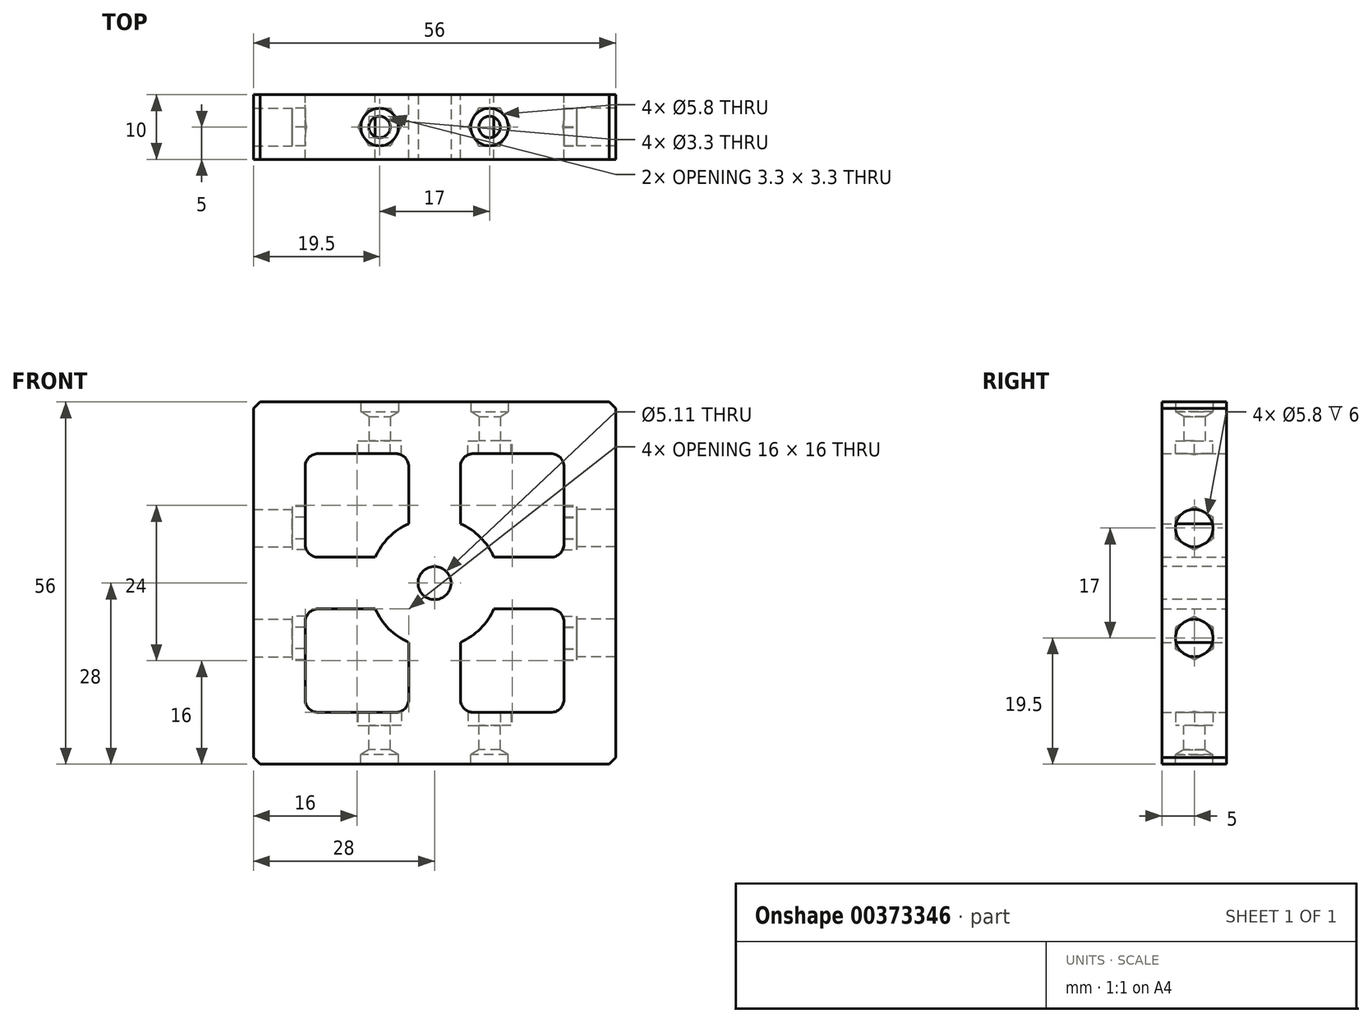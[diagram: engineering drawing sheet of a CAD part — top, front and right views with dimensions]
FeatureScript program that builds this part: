
annotation { "Feature Type Name" : "Feature", "Feature Type Description" : "" }
export const myFeature = defineFeature(function(context is Context, id is Id, definition is map)
    precondition{}
    {
        {
            var Q0;
            Q0=qCreatedBy(makeId("Front.planeOp"),FACE);
            var sketch = newSketch(context, id + "F0", { "sketchPlane" : qUnion([Q0])});
            skLineSegment(sketch, "E0.bottom", {"start": v(28, -28) * mm, "end": v(-28, -28) * mm});
            skLineSegment(sketch, "E0.top", {"start": v(28, 28) * mm, "end": v(-28, 28) * mm});
            skLineSegment(sketch, "E0.left", {"start": v(28, -28) * mm, "end": v(28, 28) * mm});
            skLineSegment(sketch, "E0.right", {"start": v(-28, -28) * mm, "end": v(-28, 28) * mm});
            skPoint(sketch, "E0.middle", {"position": v(0, 0) * mm});
            skLineSegment(sketch, "E1.bottom", {"start": v(18, -20) * mm, "end": v(6, -20) * mm});
            skLineSegment(sketch, "E1.top", {"start": v(18, 20) * mm, "end": v(6, 20) * mm});
            skLineSegment(sketch, "E1.left", {"start": v(20, -18) * mm, "end": v(20, -6) * mm});
            skLineSegment(sketch, "E1.right", {"start": v(-20, 6) * mm, "end": v(-20, 18) * mm});
            skLineSegment(sketch, "E2.left", {"start": v(4, -18) * mm, "end": v(4, 18) * mm});
            skLineSegment(sketch, "E2.right", {"start": v(-4, -18) * mm, "end": v(-4, 18) * mm});
            skLineSegment(sketch, "E3.bottom", {"start": v(18, -4) * mm, "end": v(-18, -4) * mm});
            skLineSegment(sketch, "E3.top", {"start": v(18, 4) * mm, "end": v(-18, 4) * mm});
            skPoint(sketch, "E4", {"position": v(28, -8.5) * mm});
            skPoint(sketch, "E5", {"position": v(28, 8.5) * mm});
            skPoint(sketch, "E6", {"position": v(28, 0) * mm});
            skCircle(sketch, "E7", {"center": v(0, 0) * mm, "radius": 10 * mm});
            skPoint(sketch, "E8.visualSharp", {"position": v(-20, 20) * mm});
            skArc(sketch, "E8.filletArc", {"start": v(-18, 20) * mm, "mid": v(-19.41, 19.41) * mm, "end": v(-20, 18) * mm});
            skPoint(sketch, "E9.visualSharp", {"position": v(20, 20) * mm});
            skArc(sketch, "E9.filletArc", {"start": v(20, 18) * mm, "mid": v(19.41, 19.41) * mm, "end": v(18, 20) * mm});
            skPoint(sketch, "E10.visualSharp", {"position": v(-20, -20) * mm});
            skArc(sketch, "E10.filletArc", {"start": v(-20, -18) * mm, "mid": v(-19.41, -19.41) * mm, "end": v(-18, -20) * mm});
            skPoint(sketch, "E11.visualSharp", {"position": v(20, -20) * mm});
            skArc(sketch, "E11.filletArc", {"start": v(18, -20) * mm, "mid": v(19.41, -19.41) * mm, "end": v(20, -18) * mm});
            skArc(sketch, "E12.filletArc", {"start": v(4, -18) * mm, "mid": v(4.59, -19.41) * mm, "end": v(6, -20) * mm});
            skPoint(sketch, "E13.newPointA", {"position": v(-20, 4) * mm});
            skArc(sketch, "E13.filletArc", {"start": v(-20, 6) * mm, "mid": v(-19.41, 4.59) * mm, "end": v(-18, 4) * mm});
            skArc(sketch, "E14.filletArc", {"start": v(6, 20) * mm, "mid": v(4.59, 19.41) * mm, "end": v(4, 18) * mm});
            skPoint(sketch, "E15.newPointA", {"position": v(20, -4) * mm});
            skArc(sketch, "E15.filletArc", {"start": v(20, -6) * mm, "mid": v(19.41, -4.59) * mm, "end": v(18, -4) * mm});
            skLineSegment(sketch, "E16", {"start": v(-6, -20) * mm, "end": v(-18, -20) * mm});
            skLineSegment(sketch, "E17", {"start": v(-20, -18) * mm, "end": v(-20, -6) * mm});
            skLineSegment(sketch, "E18", {"start": v(-18, 20) * mm, "end": v(-6, 20) * mm});
            skLineSegment(sketch, "E19", {"start": v(20, 18) * mm, "end": v(20, 6) * mm});
            skPoint(sketch, "E20.visualSharp", {"position": v(-4, 20) * mm});
            skArc(sketch, "E20.filletArc", {"start": v(-4, 18) * mm, "mid": v(-4.59, 19.41) * mm, "end": v(-6, 20) * mm});
            skPoint(sketch, "E21.visualSharp", {"position": v(-20, -4) * mm});
            skArc(sketch, "E21.filletArc", {"start": v(-18, -4) * mm, "mid": v(-19.41, -4.59) * mm, "end": v(-20, -6) * mm});
            skPoint(sketch, "E22.visualSharp", {"position": v(-4, -20) * mm});
            skArc(sketch, "E22.filletArc", {"start": v(-6, -20) * mm, "mid": v(-4.59, -19.41) * mm, "end": v(-4, -18) * mm});
            skPoint(sketch, "E23.visualSharp", {"position": v(20, 4) * mm});
            skArc(sketch, "E23.filletArc", {"start": v(18, 4) * mm, "mid": v(19.41, 4.59) * mm, "end": v(20, 6) * mm});
            skSolve(sketch);
        }
        {
            var Q0;
            Q0 = qSketchRegion(id + "F0", true);
            var Q1;
            {var subQ0=sQuery(id+"F0.wireOp",EDGE,"E3.top");var subQ1=sQuery(id+"F0.wireOp",EDGE,"E2.right");var subQ2=makeQuery(id+"F0.imprint","INTERSECT",VERTEX,{"derivedFrom":[subQ1,subQ0]});Q1=makeQuery(id+"F0.imprint","IMPRINT",FACE,{"disambiguationData":[TD([[makeQuery(id+"F0.imprint","IMPRINT",EDGE,{"disambiguationData":[TD([[subQ2,-1.0]])],"derivedFrom":subQ1}),1.0]])]});}
            var Q2;
            {var subQ0=sQuery(id+"F0.wireOp",EDGE,"E3.top");var subQ1=sQuery(id+"F0.wireOp",EDGE,"E2.left");var subQ2=makeQuery(id+"F0.imprint","INTERSECT",VERTEX,{"derivedFrom":[subQ1,subQ0]});Q2=makeQuery(id+"F0.imprint","IMPRINT",FACE,{"disambiguationData":[TD([[makeQuery(id+"F0.imprint","IMPRINT",EDGE,{"disambiguationData":[TD([[subQ2,-1.0]])],"derivedFrom":subQ1}),1.0]])]});}
            var Q3;
            {var subQ0=sQuery(id+"F0.wireOp",EDGE,"E3.top");var subQ1=sQuery(id+"F0.wireOp",EDGE,"E2.left");var subQ2=makeQuery(id+"F0.imprint","INTERSECT",VERTEX,{"derivedFrom":[subQ1,subQ0]});Q3=makeQuery(id+"F0.imprint","IMPRINT",FACE,{"disambiguationData":[TD([[makeQuery(id+"F0.imprint","IMPRINT",EDGE,{"disambiguationData":[TD([[subQ2,-1.0]])],"derivedFrom":subQ1}),-1.0]])]});}
            var Q4;
            {var subQ0=sQuery(id+"F0.wireOp",EDGE,"E3.bottom");var subQ1=sQuery(id+"F0.wireOp",EDGE,"E2.left");var subQ2=makeQuery(id+"F0.imprint","INTERSECT",VERTEX,{"derivedFrom":[subQ1,subQ0]});Q4=makeQuery(id+"F0.imprint","IMPRINT",FACE,{"disambiguationData":[TD([[makeQuery(id+"F0.imprint","IMPRINT",EDGE,{"disambiguationData":[TD([[subQ2,-1.0]])],"derivedFrom":subQ1}),-1.0]])]});}
            var Q5;
            {var subQ0=sQuery(id+"F0.wireOp",EDGE,"E7");var subQ1=sQuery(id+"F0.wireOp",EDGE,"E2.left");var subQ2=makeQuery(id+"F0.imprint","INTERSECT",VERTEX,{"disambiguationData":[OD(0.0)],"derivedFrom":[subQ1,subQ0]});Q5=makeQuery(id+"F0.imprint","IMPRINT",FACE,{"disambiguationData":[TD([[makeQuery(id+"F0.imprint","IMPRINT",EDGE,{"disambiguationData":[TD([[subQ2,-1.0]])],"derivedFrom":subQ1}),-1.0]])]});}
            var Q6;
            {var subQ0=sQuery(id+"F0.wireOp",EDGE,"E7");var subQ1=sQuery(id+"F0.wireOp",EDGE,"E2.left");var subQ2=makeQuery(id+"F0.imprint","INTERSECT",VERTEX,{"disambiguationData":[OD(0.0)],"derivedFrom":[subQ1,subQ0]});Q6=makeQuery(id+"F0.imprint","IMPRINT",FACE,{"disambiguationData":[TD([[makeQuery(id+"F0.imprint","IMPRINT",EDGE,{"disambiguationData":[TD([[subQ2,-1.0]])],"derivedFrom":subQ1}),1.0]])]});}
            var Q7;
            {var subQ0=sQuery(id+"F0.wireOp",EDGE,"E7");var subQ1=sQuery(id+"F0.wireOp",EDGE,"E2.right");var subQ2=makeQuery(id+"F0.imprint","INTERSECT",VERTEX,{"disambiguationData":[OD(0.0)],"derivedFrom":[subQ1,subQ0]});Q7=makeQuery(id+"F0.imprint","IMPRINT",FACE,{"disambiguationData":[TD([[makeQuery(id+"F0.imprint","IMPRINT",EDGE,{"disambiguationData":[TD([[subQ2,-1.0]])],"derivedFrom":subQ1}),1.0]])]});}
            var Q8;
            {var subQ0=sQuery(id+"F0.wireOp",EDGE,"E3.bottom");var subQ1=sQuery(id+"F0.wireOp",EDGE,"E2.right");var subQ2=makeQuery(id+"F0.imprint","INTERSECT",VERTEX,{"derivedFrom":[subQ1,subQ0]});Q8=makeQuery(id+"F0.imprint","IMPRINT",FACE,{"disambiguationData":[TD([[makeQuery(id+"F0.imprint","IMPRINT",EDGE,{"disambiguationData":[TD([[subQ2,-1.0]])],"derivedFrom":subQ1}),1.0]])]});}
            var Q9;
            {var subQ0=sQuery(id+"F0.wireOp",EDGE,"E3.bottom");var subQ1=sQuery(id+"F0.wireOp",EDGE,"E2.left");var subQ2=makeQuery(id+"F0.imprint","INTERSECT",VERTEX,{"derivedFrom":[subQ1,subQ0]});Q9=makeQuery(id+"F0.imprint","IMPRINT",FACE,{"disambiguationData":[TD([[makeQuery(id+"F0.imprint","IMPRINT",EDGE,{"disambiguationData":[TD([[subQ2,-1.0]])],"derivedFrom":subQ1}),1.0]])]});}
            extrude(context, id + "F1", {"entities" : qUnion([Q0, Q1, Q2, Q3, Q4, Q5, Q6, Q7, Q8, Q9]), "depth" : 10 * mm});
        }
        {
            var Q0;
            Q0=makeQuery(id+"F1.opExtrude","SWEPT_FACE",FACE,{"disambiguationData":[OSD([sQuery(id+"F0.wireOp",EDGE,"E0.left")])]});
            var sketch = newSketch(context, id + "F2", { "sketchPlane" : qUnion([Q0])});
            skPoint(sketch, "E24", {"position": v(-5, 8.5) * mm});
            skPoint(sketch, "E24.positionSnap0", {"position": v(-5, 28) * mm});
            skPoint(sketch, "E25", {"position": v(-5, -8.5) * mm});
            skCircle(sketch, "E26.cCircle", {"center": v(-5, 8.5) * mm, "radius": 2.9 * mm, "construction": true});
            skLineSegment(sketch, "E26.0", {"start": v(-4.96, 5.15) * mm, "end": v(-7.88, 6.79) * mm});
            skLineSegment(sketch, "E26.1", {"start": v(-7.88, 6.79) * mm, "end": v(-7.92, 10.14) * mm});
            skLineSegment(sketch, "E26.2", {"start": v(-7.92, 10.14) * mm, "end": v(-5.04, 11.85) * mm});
            skLineSegment(sketch, "E26.3", {"start": v(-5.04, 11.85) * mm, "end": v(-2.12, 10.21) * mm});
            skLineSegment(sketch, "E26.4", {"start": v(-2.12, 10.21) * mm, "end": v(-2.08, 6.86) * mm});
            skLineSegment(sketch, "E26.5", {"start": v(-2.08, 6.86) * mm, "end": v(-4.96, 5.15) * mm});
            skPoint(sketch, "E26.0.midPoint", {"position": v(-6.42, 5.97) * mm});
            skCircle(sketch, "E27.cCircle", {"center": v(-5, -8.5) * mm, "radius": 2.9 * mm, "construction": true});
            skLineSegment(sketch, "E27.0", {"start": v(-4.96, -11.85) * mm, "end": v(-7.88, -10.21) * mm});
            skLineSegment(sketch, "E27.1", {"start": v(-7.88, -10.21) * mm, "end": v(-7.92, -6.86) * mm});
            skLineSegment(sketch, "E27.2", {"start": v(-7.92, -6.86) * mm, "end": v(-5.04, -5.15) * mm});
            skLineSegment(sketch, "E27.3", {"start": v(-5.04, -5.15) * mm, "end": v(-2.12, -6.79) * mm});
            skLineSegment(sketch, "E27.4", {"start": v(-2.12, -6.79) * mm, "end": v(-2.08, -10.14) * mm});
            skLineSegment(sketch, "E27.5", {"start": v(-2.08, -10.14) * mm, "end": v(-4.96, -11.85) * mm});
            skSolve(sketch);
        }
        {
            var Q0;
            Q0 = qSketchRegion(id + "F2", true);
            extrude(context, id + "F3", {"entities" : qUnion([Q0]), "operationType" : NewBodyOperationType.REMOVE, "oppositeDirection" : true, "depth" : 10 * mm, "hasSecondDirection" : true, "secondDirectionOppositeDirection" : true, "secondDirectionDepth" : 6 * mm});
        }
        {
            var Q0;
            Q0=sQuery(id+"F2.wireOp",VERTEX,"E25");
            var Q1;
            Q1=sQuery(id+"F2.wireOp",VERTEX,"E24");
            var Q2;
            Q2=makeQuery(id+"F1.opExtrude","SWEPT_BODY",BODY,{"disambiguationData":[OSD([sQuery(id+"F0.wireOp",EDGE,"E0.bottom"),sQuery(id+"F0.wireOp",EDGE,"E0.top"),sQuery(id+"F0.wireOp",EDGE,"E0.left"),sQuery(id+"F0.wireOp",EDGE,"E0.right"),sQuery(id+"F0.wireOp",EDGE,"E1.bottom"),sQuery(id+"F0.wireOp",EDGE,"E1.top"),sQuery(id+"F0.wireOp",EDGE,"E1.left"),sQuery(id+"F0.wireOp",EDGE,"E1.right"),sQuery(id+"F0.wireOp",EDGE,"E2.left"),sQuery(id+"F0.wireOp",EDGE,"E2.right"),sQuery(id+"F0.wireOp",EDGE,"E3.bottom"),sQuery(id+"F0.wireOp",EDGE,"E3.top"),sQuery(id+"F0.wireOp",EDGE,"E7"),sQuery(id+"F0.wireOp",EDGE,"E8.filletArc"),sQuery(id+"F0.wireOp",EDGE,"E9.filletArc"),sQuery(id+"F0.wireOp",EDGE,"E10.filletArc"),sQuery(id+"F0.wireOp",EDGE,"E11.filletArc"),sQuery(id+"F0.wireOp",EDGE,"E12.filletArc"),sQuery(id+"F0.wireOp",EDGE,"E13.filletArc"),sQuery(id+"F0.wireOp",EDGE,"E14.filletArc"),sQuery(id+"F0.wireOp",EDGE,"E15.filletArc"),sQuery(id+"F0.wireOp",EDGE,"E16"),sQuery(id+"F0.wireOp",EDGE,"E17"),sQuery(id+"F0.wireOp",EDGE,"E18"),sQuery(id+"F0.wireOp",EDGE,"E19"),sQuery(id+"F0.wireOp",EDGE,"E20.filletArc"),sQuery(id+"F0.wireOp",EDGE,"E21.filletArc"),sQuery(id+"F0.wireOp",EDGE,"E22.filletArc"),sQuery(id+"F0.wireOp",EDGE,"E23.filletArc")])]});
            hole(context, id + "F4", {"style" : HoleStyle.SIMPLE, "endStyle" : HoleEndStyle.BLIND, "standardTappedOrClearance" : lookupTablePath({ "standard" : "ISO", "fit" : "Normal", "size" : "M3", "type" : "Clearance" }), "standardBlindInLast" : lookupTablePath({ "fit" : "Standard", "standard" : "ISO", "size" : "M3", "type" : "Clearance" }), "holeDiameter" : 3.3 * mm, "holeDepth" : 10 * mm, "tappedDepth" : 12 * mm, "tapClearance" : 3, "locations" : qUnion([Q0, Q1]), "scope" : qUnion([Q2])});
        }
        {
            var Q0;
            Q0=sQuery(id+"F2.wireOp",VERTEX,"E24");
            var Q1;
            Q1=sQuery(id+"F2.wireOp",VERTEX,"E25");
            var Q2;
            Q2=makeQuery(id+"F1.opExtrude","SWEPT_BODY",BODY,{"disambiguationData":[OSD([sQuery(id+"F0.wireOp",EDGE,"E0.bottom"),sQuery(id+"F0.wireOp",EDGE,"E0.top"),sQuery(id+"F0.wireOp",EDGE,"E0.left"),sQuery(id+"F0.wireOp",EDGE,"E0.right"),sQuery(id+"F0.wireOp",EDGE,"E1.bottom"),sQuery(id+"F0.wireOp",EDGE,"E1.top"),sQuery(id+"F0.wireOp",EDGE,"E1.left"),sQuery(id+"F0.wireOp",EDGE,"E1.right"),sQuery(id+"F0.wireOp",EDGE,"E2.left"),sQuery(id+"F0.wireOp",EDGE,"E2.right"),sQuery(id+"F0.wireOp",EDGE,"E3.bottom"),sQuery(id+"F0.wireOp",EDGE,"E3.top"),sQuery(id+"F0.wireOp",EDGE,"E7"),sQuery(id+"F0.wireOp",EDGE,"E8.filletArc"),sQuery(id+"F0.wireOp",EDGE,"E9.filletArc"),sQuery(id+"F0.wireOp",EDGE,"E10.filletArc"),sQuery(id+"F0.wireOp",EDGE,"E11.filletArc"),sQuery(id+"F0.wireOp",EDGE,"E12.filletArc"),sQuery(id+"F0.wireOp",EDGE,"E13.filletArc"),sQuery(id+"F0.wireOp",EDGE,"E14.filletArc"),sQuery(id+"F0.wireOp",EDGE,"E15.filletArc"),sQuery(id+"F0.wireOp",EDGE,"E16"),sQuery(id+"F0.wireOp",EDGE,"E17"),sQuery(id+"F0.wireOp",EDGE,"E18"),sQuery(id+"F0.wireOp",EDGE,"E19"),sQuery(id+"F0.wireOp",EDGE,"E20.filletArc"),sQuery(id+"F0.wireOp",EDGE,"E21.filletArc"),sQuery(id+"F0.wireOp",EDGE,"E22.filletArc"),sQuery(id+"F0.wireOp",EDGE,"E23.filletArc")])]});
            hole(context, id + "F5", {"style" : HoleStyle.SIMPLE, "endStyle" : HoleEndStyle.BLIND, "holeDiameter" : 5.8 * mm, "holeDepth" : 1.5 * mm, "tappedDepth" : 12 * mm, "tapClearance" : 3, "locations" : qUnion([Q0, Q1]), "scope" : qUnion([Q2])});
        }
        {
            var Q0;
            Q0=makeQuery(id+"F1.opExtrude","SWEPT_FACE",FACE,{"disambiguationData":[OSD([sQuery(id+"F0.wireOp",EDGE,"E0.bottom")])]});
            var sketch = newSketch(context, id + "F6", { "sketchPlane" : qUnion([Q0])});
            skPoint(sketch, "E28", {"position": v(8.5, 5) * mm});
            skPoint(sketch, "E28.positionSnap0", {"position": v(28, 5) * mm});
            skPoint(sketch, "E29", {"position": v(-8.5, 5) * mm});
            skPoint(sketch, "E29.positionSnap0", {"position": v(-28, 5) * mm});
            skCircle(sketch, "E30.cCircle", {"center": v(8.5, 5) * mm, "radius": 2.9 * mm, "construction": true});
            skLineSegment(sketch, "E30.0", {"start": v(5.15, 5) * mm, "end": v(6.83, 7.9) * mm});
            skLineSegment(sketch, "E30.1", {"start": v(6.83, 7.9) * mm, "end": v(10.17, 7.9) * mm});
            skLineSegment(sketch, "E30.2", {"start": v(10.17, 7.9) * mm, "end": v(11.85, 5) * mm});
            skLineSegment(sketch, "E30.3", {"start": v(11.85, 5) * mm, "end": v(10.17, 2.1) * mm});
            skLineSegment(sketch, "E30.4", {"start": v(10.17, 2.1) * mm, "end": v(6.83, 2.1) * mm});
            skLineSegment(sketch, "E30.5", {"start": v(6.83, 2.1) * mm, "end": v(5.15, 5) * mm});
            skPoint(sketch, "E30.0.midPoint", {"position": v(5.99, 6.45) * mm});
            skCircle(sketch, "E31.cCircle", {"center": v(-8.5, 5) * mm, "radius": 2.9 * mm, "construction": true});
            skLineSegment(sketch, "E31.0", {"start": v(-11.85, 5) * mm, "end": v(-10.17, 7.9) * mm});
            skLineSegment(sketch, "E31.1", {"start": v(-10.17, 7.9) * mm, "end": v(-6.83, 7.9) * mm});
            skLineSegment(sketch, "E31.2", {"start": v(-6.83, 7.9) * mm, "end": v(-5.15, 5) * mm});
            skLineSegment(sketch, "E31.3", {"start": v(-5.15, 5) * mm, "end": v(-6.83, 2.1) * mm});
            skLineSegment(sketch, "E31.4", {"start": v(-6.83, 2.1) * mm, "end": v(-10.17, 2.1) * mm});
            skLineSegment(sketch, "E31.5", {"start": v(-10.17, 2.1) * mm, "end": v(-11.85, 5) * mm});
            skPoint(sketch, "E31.0.midPoint", {"position": v(-11.01, 6.45) * mm});
            skSolve(sketch);
        }
        {
            var Q0;
            Q0 = qSketchRegion(id + "F6", true);
            extrude(context, id + "F7", {"entities" : qUnion([Q0]), "operationType" : NewBodyOperationType.REMOVE, "oppositeDirection" : true, "depth" : 10 * mm, "hasSecondDirection" : true, "secondDirectionOppositeDirection" : true, "secondDirectionDepth" : 6 * mm});
        }
        {
            var Q0;
            Q0=sQuery(id+"F6.wireOp",VERTEX,"E28");
            var Q1;
            Q1=sQuery(id+"F6.wireOp",VERTEX,"E29");
            var Q2;
            Q2=makeQuery(id+"F1.opExtrude","SWEPT_BODY",BODY,{"disambiguationData":[OSD([sQuery(id+"F0.wireOp",EDGE,"E0.bottom"),sQuery(id+"F0.wireOp",EDGE,"E0.top"),sQuery(id+"F0.wireOp",EDGE,"E0.left"),sQuery(id+"F0.wireOp",EDGE,"E0.right"),sQuery(id+"F0.wireOp",EDGE,"E1.bottom"),sQuery(id+"F0.wireOp",EDGE,"E1.top"),sQuery(id+"F0.wireOp",EDGE,"E1.left"),sQuery(id+"F0.wireOp",EDGE,"E1.right"),sQuery(id+"F0.wireOp",EDGE,"E2.left"),sQuery(id+"F0.wireOp",EDGE,"E2.right"),sQuery(id+"F0.wireOp",EDGE,"E3.bottom"),sQuery(id+"F0.wireOp",EDGE,"E3.top"),sQuery(id+"F0.wireOp",EDGE,"E7"),sQuery(id+"F0.wireOp",EDGE,"E8.filletArc"),sQuery(id+"F0.wireOp",EDGE,"E9.filletArc"),sQuery(id+"F0.wireOp",EDGE,"E10.filletArc"),sQuery(id+"F0.wireOp",EDGE,"E11.filletArc"),sQuery(id+"F0.wireOp",EDGE,"E12.filletArc"),sQuery(id+"F0.wireOp",EDGE,"E13.filletArc"),sQuery(id+"F0.wireOp",EDGE,"E14.filletArc"),sQuery(id+"F0.wireOp",EDGE,"E15.filletArc"),sQuery(id+"F0.wireOp",EDGE,"E16"),sQuery(id+"F0.wireOp",EDGE,"E17"),sQuery(id+"F0.wireOp",EDGE,"E18"),sQuery(id+"F0.wireOp",EDGE,"E19"),sQuery(id+"F0.wireOp",EDGE,"E20.filletArc"),sQuery(id+"F0.wireOp",EDGE,"E21.filletArc"),sQuery(id+"F0.wireOp",EDGE,"E22.filletArc"),sQuery(id+"F0.wireOp",EDGE,"E23.filletArc")])]});
            hole(context, id + "F8", {"style" : HoleStyle.SIMPLE, "endStyle" : HoleEndStyle.BLIND, "holeDiameter" : 5.8 * mm, "holeDepth" : 1.5 * mm, "tappedDepth" : 12 * mm, "tapClearance" : 3, "locations" : qUnion([Q0, Q1]), "scope" : qUnion([Q2])});
        }
        {
            var Q0;
            Q0=sQuery(id+"F6.wireOp",VERTEX,"E28");
            var Q1;
            Q1=sQuery(id+"F6.wireOp",VERTEX,"E29");
            var Q2;
            Q2=makeQuery(id+"F1.opExtrude","SWEPT_BODY",BODY,{"disambiguationData":[OSD([sQuery(id+"F0.wireOp",EDGE,"E0.bottom"),sQuery(id+"F0.wireOp",EDGE,"E0.top"),sQuery(id+"F0.wireOp",EDGE,"E0.left"),sQuery(id+"F0.wireOp",EDGE,"E0.right"),sQuery(id+"F0.wireOp",EDGE,"E1.bottom"),sQuery(id+"F0.wireOp",EDGE,"E1.top"),sQuery(id+"F0.wireOp",EDGE,"E1.left"),sQuery(id+"F0.wireOp",EDGE,"E1.right"),sQuery(id+"F0.wireOp",EDGE,"E2.left"),sQuery(id+"F0.wireOp",EDGE,"E2.right"),sQuery(id+"F0.wireOp",EDGE,"E3.bottom"),sQuery(id+"F0.wireOp",EDGE,"E3.top"),sQuery(id+"F0.wireOp",EDGE,"E7"),sQuery(id+"F0.wireOp",EDGE,"E8.filletArc"),sQuery(id+"F0.wireOp",EDGE,"E9.filletArc"),sQuery(id+"F0.wireOp",EDGE,"E10.filletArc"),sQuery(id+"F0.wireOp",EDGE,"E11.filletArc"),sQuery(id+"F0.wireOp",EDGE,"E12.filletArc"),sQuery(id+"F0.wireOp",EDGE,"E13.filletArc"),sQuery(id+"F0.wireOp",EDGE,"E14.filletArc"),sQuery(id+"F0.wireOp",EDGE,"E15.filletArc"),sQuery(id+"F0.wireOp",EDGE,"E16"),sQuery(id+"F0.wireOp",EDGE,"E17"),sQuery(id+"F0.wireOp",EDGE,"E18"),sQuery(id+"F0.wireOp",EDGE,"E19"),sQuery(id+"F0.wireOp",EDGE,"E20.filletArc"),sQuery(id+"F0.wireOp",EDGE,"E21.filletArc"),sQuery(id+"F0.wireOp",EDGE,"E22.filletArc"),sQuery(id+"F0.wireOp",EDGE,"E23.filletArc")])]});
            hole(context, id + "F9", {"style" : HoleStyle.SIMPLE, "endStyle" : HoleEndStyle.BLIND, "standardTappedOrClearance" : lookupTablePath({ "standard" : "ISO", "fit" : "Normal", "size" : "M3", "type" : "Clearance" }), "standardBlindInLast" : lookupTablePath({ "fit" : "Standard", "standard" : "ISO", "size" : "M3", "type" : "Clearance" }), "holeDiameter" : 3.3 * mm, "holeDepth" : 10 * mm, "tappedDepth" : 12 * mm, "tapClearance" : 3, "locations" : qUnion([Q0, Q1]), "scope" : qUnion([Q2])});
        }
        {
            var Q0;
            Q0=makeQuery(id+"F1.opExtrude","SWEPT_FACE",FACE,{"disambiguationData":[OSD([sQuery(id+"F0.wireOp",EDGE,"E0.right")])]});
            var sketch = newSketch(context, id + "F10", { "sketchPlane" : qUnion([Q0])});
            skPoint(sketch, "E32", {"position": v(5, -8.5) * mm});
            skPoint(sketch, "E32.positionSnap0", {"position": v(5, -28) * mm});
            skPoint(sketch, "E33", {"position": v(5, 28) * mm});
            skPoint(sketch, "E34", {"position": v(5, 8.5) * mm});
            skCircle(sketch, "E35.cCircle", {"center": v(5, -8.5) * mm, "radius": 2.9 * mm, "construction": true});
            skLineSegment(sketch, "E35.0", {"start": v(5, -5.15) * mm, "end": v(7.9, -6.83) * mm});
            skLineSegment(sketch, "E35.1", {"start": v(7.9, -6.83) * mm, "end": v(7.9, -10.17) * mm});
            skLineSegment(sketch, "E35.2", {"start": v(7.9, -10.17) * mm, "end": v(5, -11.85) * mm});
            skLineSegment(sketch, "E35.3", {"start": v(5, -11.85) * mm, "end": v(2.1, -10.17) * mm});
            skLineSegment(sketch, "E35.4", {"start": v(2.1, -10.17) * mm, "end": v(2.1, -6.83) * mm});
            skLineSegment(sketch, "E35.5", {"start": v(2.1, -6.83) * mm, "end": v(5, -5.15) * mm});
            skPoint(sketch, "E35.0.midPoint", {"position": v(6.45, -5.99) * mm});
            skCircle(sketch, "E36.cCircle", {"center": v(5, 8.5) * mm, "radius": 2.9 * mm, "construction": true});
            skLineSegment(sketch, "E36.0", {"start": v(5, 11.85) * mm, "end": v(7.9, 10.17) * mm});
            skLineSegment(sketch, "E36.1", {"start": v(7.9, 10.17) * mm, "end": v(7.9, 6.83) * mm});
            skLineSegment(sketch, "E36.2", {"start": v(7.9, 6.83) * mm, "end": v(5, 5.15) * mm});
            skLineSegment(sketch, "E36.3", {"start": v(5, 5.15) * mm, "end": v(2.1, 6.83) * mm});
            skLineSegment(sketch, "E36.4", {"start": v(2.1, 6.83) * mm, "end": v(2.1, 10.17) * mm});
            skLineSegment(sketch, "E36.5", {"start": v(2.1, 10.17) * mm, "end": v(5, 11.85) * mm});
            skPoint(sketch, "E36.0.midPoint", {"position": v(6.45, 11.01) * mm});
            skSolve(sketch);
        }
        {
            var Q0;
            Q0 = qSketchRegion(id + "F10", true);
            extrude(context, id + "F11", {"entities" : qUnion([Q0]), "operationType" : NewBodyOperationType.REMOVE, "oppositeDirection" : true, "depth" : 10 * mm, "hasSecondDirection" : true, "secondDirectionOppositeDirection" : true, "secondDirectionDepth" : 6 * mm});
        }
        {
            var Q0;
            Q0=sQuery(id+"F10.wireOp",VERTEX,"E32");
            var Q1;
            Q1=sQuery(id+"F10.wireOp",VERTEX,"E34");
            var Q2;
            Q2=makeQuery(id+"F1.opExtrude","SWEPT_BODY",BODY,{"disambiguationData":[OSD([sQuery(id+"F0.wireOp",EDGE,"E0.bottom"),sQuery(id+"F0.wireOp",EDGE,"E0.top"),sQuery(id+"F0.wireOp",EDGE,"E0.left"),sQuery(id+"F0.wireOp",EDGE,"E0.right"),sQuery(id+"F0.wireOp",EDGE,"E1.bottom"),sQuery(id+"F0.wireOp",EDGE,"E1.top"),sQuery(id+"F0.wireOp",EDGE,"E1.left"),sQuery(id+"F0.wireOp",EDGE,"E1.right"),sQuery(id+"F0.wireOp",EDGE,"E2.left"),sQuery(id+"F0.wireOp",EDGE,"E2.right"),sQuery(id+"F0.wireOp",EDGE,"E3.bottom"),sQuery(id+"F0.wireOp",EDGE,"E3.top"),sQuery(id+"F0.wireOp",EDGE,"E7"),sQuery(id+"F0.wireOp",EDGE,"E8.filletArc"),sQuery(id+"F0.wireOp",EDGE,"E9.filletArc"),sQuery(id+"F0.wireOp",EDGE,"E10.filletArc"),sQuery(id+"F0.wireOp",EDGE,"E11.filletArc"),sQuery(id+"F0.wireOp",EDGE,"E12.filletArc"),sQuery(id+"F0.wireOp",EDGE,"E13.filletArc"),sQuery(id+"F0.wireOp",EDGE,"E14.filletArc"),sQuery(id+"F0.wireOp",EDGE,"E15.filletArc"),sQuery(id+"F0.wireOp",EDGE,"E16"),sQuery(id+"F0.wireOp",EDGE,"E17"),sQuery(id+"F0.wireOp",EDGE,"E18"),sQuery(id+"F0.wireOp",EDGE,"E19"),sQuery(id+"F0.wireOp",EDGE,"E20.filletArc"),sQuery(id+"F0.wireOp",EDGE,"E21.filletArc"),sQuery(id+"F0.wireOp",EDGE,"E22.filletArc"),sQuery(id+"F0.wireOp",EDGE,"E23.filletArc")])]});
            hole(context, id + "F12", {"style" : HoleStyle.SIMPLE, "endStyle" : HoleEndStyle.BLIND, "standardTappedOrClearance" : lookupTablePath({ "standard" : "ISO", "fit" : "Normal", "size" : "M3", "type" : "Clearance" }), "standardBlindInLast" : lookupTablePath({ "fit" : "Standard", "standard" : "ISO", "size" : "M3", "type" : "Clearance" }), "holeDiameter" : 3.3 * mm, "holeDepth" : 10 * mm, "tappedDepth" : 12 * mm, "tapClearance" : 3, "locations" : qUnion([Q0, Q1]), "scope" : qUnion([Q2])});
        }
        {
            var Q0;
            Q0=sQuery(id+"F10.wireOp",VERTEX,"E32");
            var Q1;
            Q1=sQuery(id+"F10.wireOp",VERTEX,"E34");
            var Q2;
            Q2=makeQuery(id+"F1.opExtrude","SWEPT_BODY",BODY,{"disambiguationData":[OSD([sQuery(id+"F0.wireOp",EDGE,"E0.bottom"),sQuery(id+"F0.wireOp",EDGE,"E0.top"),sQuery(id+"F0.wireOp",EDGE,"E0.left"),sQuery(id+"F0.wireOp",EDGE,"E0.right"),sQuery(id+"F0.wireOp",EDGE,"E1.bottom"),sQuery(id+"F0.wireOp",EDGE,"E1.top"),sQuery(id+"F0.wireOp",EDGE,"E1.left"),sQuery(id+"F0.wireOp",EDGE,"E1.right"),sQuery(id+"F0.wireOp",EDGE,"E2.left"),sQuery(id+"F0.wireOp",EDGE,"E2.right"),sQuery(id+"F0.wireOp",EDGE,"E3.bottom"),sQuery(id+"F0.wireOp",EDGE,"E3.top"),sQuery(id+"F0.wireOp",EDGE,"E7"),sQuery(id+"F0.wireOp",EDGE,"E8.filletArc"),sQuery(id+"F0.wireOp",EDGE,"E9.filletArc"),sQuery(id+"F0.wireOp",EDGE,"E10.filletArc"),sQuery(id+"F0.wireOp",EDGE,"E11.filletArc"),sQuery(id+"F0.wireOp",EDGE,"E12.filletArc"),sQuery(id+"F0.wireOp",EDGE,"E13.filletArc"),sQuery(id+"F0.wireOp",EDGE,"E14.filletArc"),sQuery(id+"F0.wireOp",EDGE,"E15.filletArc"),sQuery(id+"F0.wireOp",EDGE,"E16"),sQuery(id+"F0.wireOp",EDGE,"E17"),sQuery(id+"F0.wireOp",EDGE,"E18"),sQuery(id+"F0.wireOp",EDGE,"E19"),sQuery(id+"F0.wireOp",EDGE,"E20.filletArc"),sQuery(id+"F0.wireOp",EDGE,"E21.filletArc"),sQuery(id+"F0.wireOp",EDGE,"E22.filletArc"),sQuery(id+"F0.wireOp",EDGE,"E23.filletArc")])]});
            hole(context, id + "F13", {"style" : HoleStyle.SIMPLE, "endStyle" : HoleEndStyle.BLIND, "holeDiameter" : 5.8 * mm, "holeDepth" : 1.5 * mm, "tappedDepth" : 12 * mm, "tapClearance" : 3, "locations" : qUnion([Q0, Q1]), "scope" : qUnion([Q2])});
        }
        {
            var Q0;
            Q0=makeQuery(id+"F1.opExtrude","SWEPT_FACE",FACE,{"disambiguationData":[OSD([sQuery(id+"F0.wireOp",EDGE,"E0.top")])]});
            var sketch = newSketch(context, id + "F14", { "sketchPlane" : qUnion([Q0])});
            skPoint(sketch, "E37", {"position": v(-8.5, -5) * mm});
            skPoint(sketch, "E37.positionSnap0", {"position": v(-28, -5) * mm});
            skPoint(sketch, "E38", {"position": v(8.5, -5) * mm});
            skPoint(sketch, "E38.positionSnap0", {"position": v(28, -5) * mm});
            skCircle(sketch, "E39.cCircle", {"center": v(-8.5, -5) * mm, "radius": 2.9 * mm, "construction": true});
            skLineSegment(sketch, "E39.0", {"start": v(-5.15, -5) * mm, "end": v(-6.83, -7.9) * mm});
            skLineSegment(sketch, "E39.1", {"start": v(-6.83, -7.9) * mm, "end": v(-10.17, -7.9) * mm});
            skLineSegment(sketch, "E39.2", {"start": v(-10.17, -7.9) * mm, "end": v(-11.85, -5) * mm});
            skLineSegment(sketch, "E39.3", {"start": v(-11.85, -5) * mm, "end": v(-10.17, -2.1) * mm});
            skLineSegment(sketch, "E39.4", {"start": v(-10.17, -2.1) * mm, "end": v(-6.83, -2.1) * mm});
            skLineSegment(sketch, "E39.5", {"start": v(-6.83, -2.1) * mm, "end": v(-5.15, -5) * mm});
            skPoint(sketch, "E39.0.midPoint", {"position": v(-5.99, -6.45) * mm});
            skCircle(sketch, "E40.cCircle", {"center": v(8.5, -5) * mm, "radius": 2.9 * mm, "construction": true});
            skLineSegment(sketch, "E40.0", {"start": v(10.17, -7.9) * mm, "end": v(6.83, -7.9) * mm});
            skLineSegment(sketch, "E40.1", {"start": v(6.83, -7.9) * mm, "end": v(5.15, -5) * mm});
            skLineSegment(sketch, "E40.2", {"start": v(5.15, -5) * mm, "end": v(6.83, -2.1) * mm});
            skLineSegment(sketch, "E40.3", {"start": v(6.83, -2.1) * mm, "end": v(10.17, -2.1) * mm});
            skLineSegment(sketch, "E40.4", {"start": v(10.17, -2.1) * mm, "end": v(11.85, -5) * mm});
            skLineSegment(sketch, "E40.5", {"start": v(11.85, -5) * mm, "end": v(10.17, -7.9) * mm});
            skPoint(sketch, "E40.0.midPoint", {"position": v(8.5, -7.9) * mm});
            skSolve(sketch);
        }
        {
            var Q0;
            Q0 = qSketchRegion(id + "F14", true);
            extrude(context, id + "F15", {"entities" : qUnion([Q0]), "operationType" : NewBodyOperationType.REMOVE, "oppositeDirection" : true, "depth" : 10 * mm, "hasSecondDirection" : true, "secondDirectionOppositeDirection" : true, "secondDirectionDepth" : 6 * mm});
        }
        {
            var Q0;
            Q0=sQuery(id+"F14.wireOp",VERTEX,"E37");
            var Q1;
            Q1=sQuery(id+"F14.wireOp",VERTEX,"E38");
            var Q2;
            Q2=makeQuery(id+"F1.opExtrude","SWEPT_BODY",BODY,{"disambiguationData":[OSD([sQuery(id+"F0.wireOp",EDGE,"E0.bottom"),sQuery(id+"F0.wireOp",EDGE,"E0.top"),sQuery(id+"F0.wireOp",EDGE,"E0.left"),sQuery(id+"F0.wireOp",EDGE,"E0.right"),sQuery(id+"F0.wireOp",EDGE,"E1.bottom"),sQuery(id+"F0.wireOp",EDGE,"E1.top"),sQuery(id+"F0.wireOp",EDGE,"E1.left"),sQuery(id+"F0.wireOp",EDGE,"E1.right"),sQuery(id+"F0.wireOp",EDGE,"E2.left"),sQuery(id+"F0.wireOp",EDGE,"E2.right"),sQuery(id+"F0.wireOp",EDGE,"E3.bottom"),sQuery(id+"F0.wireOp",EDGE,"E3.top"),sQuery(id+"F0.wireOp",EDGE,"E7"),sQuery(id+"F0.wireOp",EDGE,"E8.filletArc"),sQuery(id+"F0.wireOp",EDGE,"E9.filletArc"),sQuery(id+"F0.wireOp",EDGE,"E10.filletArc"),sQuery(id+"F0.wireOp",EDGE,"E11.filletArc"),sQuery(id+"F0.wireOp",EDGE,"E12.filletArc"),sQuery(id+"F0.wireOp",EDGE,"E13.filletArc"),sQuery(id+"F0.wireOp",EDGE,"E14.filletArc"),sQuery(id+"F0.wireOp",EDGE,"E15.filletArc"),sQuery(id+"F0.wireOp",EDGE,"E16"),sQuery(id+"F0.wireOp",EDGE,"E17"),sQuery(id+"F0.wireOp",EDGE,"E18"),sQuery(id+"F0.wireOp",EDGE,"E19"),sQuery(id+"F0.wireOp",EDGE,"E20.filletArc"),sQuery(id+"F0.wireOp",EDGE,"E21.filletArc"),sQuery(id+"F0.wireOp",EDGE,"E22.filletArc"),sQuery(id+"F0.wireOp",EDGE,"E23.filletArc")])]});
            hole(context, id + "F16", {"style" : HoleStyle.SIMPLE, "endStyle" : HoleEndStyle.BLIND, "holeDiameter" : 5.8 * mm, "holeDepth" : 1.5 * mm, "tappedDepth" : 12 * mm, "tapClearance" : 3, "locations" : qUnion([Q0, Q1]), "scope" : qUnion([Q2])});
        }
        {
            var Q0;
            Q0=sQuery(id+"F14.wireOp",VERTEX,"E37");
            var Q1;
            Q1=sQuery(id+"F14.wireOp",VERTEX,"E38");
            var Q2;
            Q2=makeQuery(id+"F1.opExtrude","SWEPT_BODY",BODY,{"disambiguationData":[OSD([sQuery(id+"F0.wireOp",EDGE,"E0.bottom"),sQuery(id+"F0.wireOp",EDGE,"E0.top"),sQuery(id+"F0.wireOp",EDGE,"E0.left"),sQuery(id+"F0.wireOp",EDGE,"E0.right"),sQuery(id+"F0.wireOp",EDGE,"E1.bottom"),sQuery(id+"F0.wireOp",EDGE,"E1.top"),sQuery(id+"F0.wireOp",EDGE,"E1.left"),sQuery(id+"F0.wireOp",EDGE,"E1.right"),sQuery(id+"F0.wireOp",EDGE,"E2.left"),sQuery(id+"F0.wireOp",EDGE,"E2.right"),sQuery(id+"F0.wireOp",EDGE,"E3.bottom"),sQuery(id+"F0.wireOp",EDGE,"E3.top"),sQuery(id+"F0.wireOp",EDGE,"E7"),sQuery(id+"F0.wireOp",EDGE,"E8.filletArc"),sQuery(id+"F0.wireOp",EDGE,"E9.filletArc"),sQuery(id+"F0.wireOp",EDGE,"E10.filletArc"),sQuery(id+"F0.wireOp",EDGE,"E11.filletArc"),sQuery(id+"F0.wireOp",EDGE,"E12.filletArc"),sQuery(id+"F0.wireOp",EDGE,"E13.filletArc"),sQuery(id+"F0.wireOp",EDGE,"E14.filletArc"),sQuery(id+"F0.wireOp",EDGE,"E15.filletArc"),sQuery(id+"F0.wireOp",EDGE,"E16"),sQuery(id+"F0.wireOp",EDGE,"E17"),sQuery(id+"F0.wireOp",EDGE,"E18"),sQuery(id+"F0.wireOp",EDGE,"E19"),sQuery(id+"F0.wireOp",EDGE,"E20.filletArc"),sQuery(id+"F0.wireOp",EDGE,"E21.filletArc"),sQuery(id+"F0.wireOp",EDGE,"E22.filletArc"),sQuery(id+"F0.wireOp",EDGE,"E23.filletArc")])]});
            hole(context, id + "F17", {"style" : HoleStyle.SIMPLE, "endStyle" : HoleEndStyle.BLIND, "standardTappedOrClearance" : lookupTablePath({ "standard" : "ISO", "fit" : "Normal", "size" : "M3", "type" : "Clearance" }), "standardBlindInLast" : lookupTablePath({ "fit" : "Standard", "standard" : "ISO", "size" : "M3", "type" : "Clearance" }), "holeDiameter" : 3.3 * mm, "holeDepth" : 10 * mm, "tappedDepth" : 12 * mm, "tapClearance" : 3, "locations" : qUnion([Q0, Q1]), "scope" : qUnion([Q2])});
        }
        {
            var Q0;
            Q0=makeQuery(id+"F1.opExtrude","SWEPT_EDGE",EDGE,{"disambiguationData":[OSD([sQuery(id+"F0.wireOp",EDGE,"E0.top"),sQuery(id+"F0.wireOp",EDGE,"E0.left")])]});
            var Q1;
            Q1=makeQuery(id+"F1.opExtrude","SWEPT_EDGE",EDGE,{"disambiguationData":[OSD([sQuery(id+"F0.wireOp",EDGE,"E0.bottom"),sQuery(id+"F0.wireOp",EDGE,"E0.left")])]});
            var Q2;
            Q2=makeQuery(id+"F1.opExtrude","SWEPT_EDGE",EDGE,{"disambiguationData":[OSD([sQuery(id+"F0.wireOp",EDGE,"E0.bottom"),sQuery(id+"F0.wireOp",EDGE,"E0.right")])]});
            var Q3;
            Q3=makeQuery(id+"F1.opExtrude","SWEPT_EDGE",EDGE,{"disambiguationData":[OSD([sQuery(id+"F0.wireOp",EDGE,"E0.top"),sQuery(id+"F0.wireOp",EDGE,"E0.right")])]});
            chamfer(context, id + "F18", {"entities" : qUnion([Q0, Q1, Q2, Q3]), "width" : 1 * mm, "tangentPropagation" : true});
        }
        {
            var Q0;
            Q0=sQuery(id+"F0.wireOp",VERTEX,"E7.center");
            var Q1;
            Q1=makeQuery(id+"F1.opExtrude","SWEPT_BODY",BODY,{"disambiguationData":[OSD([sQuery(id+"F0.wireOp",EDGE,"E0.bottom"),sQuery(id+"F0.wireOp",EDGE,"E0.top"),sQuery(id+"F0.wireOp",EDGE,"E0.left"),sQuery(id+"F0.wireOp",EDGE,"E0.right"),sQuery(id+"F0.wireOp",EDGE,"E1.bottom"),sQuery(id+"F0.wireOp",EDGE,"E1.top"),sQuery(id+"F0.wireOp",EDGE,"E1.left"),sQuery(id+"F0.wireOp",EDGE,"E1.right"),sQuery(id+"F0.wireOp",EDGE,"E2.left"),sQuery(id+"F0.wireOp",EDGE,"E2.right"),sQuery(id+"F0.wireOp",EDGE,"E3.bottom"),sQuery(id+"F0.wireOp",EDGE,"E3.top"),sQuery(id+"F0.wireOp",EDGE,"E7"),sQuery(id+"F0.wireOp",EDGE,"E8.filletArc"),sQuery(id+"F0.wireOp",EDGE,"E9.filletArc"),sQuery(id+"F0.wireOp",EDGE,"E10.filletArc"),sQuery(id+"F0.wireOp",EDGE,"E11.filletArc"),sQuery(id+"F0.wireOp",EDGE,"E12.filletArc"),sQuery(id+"F0.wireOp",EDGE,"E13.filletArc"),sQuery(id+"F0.wireOp",EDGE,"E14.filletArc"),sQuery(id+"F0.wireOp",EDGE,"E15.filletArc"),sQuery(id+"F0.wireOp",EDGE,"E16"),sQuery(id+"F0.wireOp",EDGE,"E17"),sQuery(id+"F0.wireOp",EDGE,"E18"),sQuery(id+"F0.wireOp",EDGE,"E19"),sQuery(id+"F0.wireOp",EDGE,"E20.filletArc"),sQuery(id+"F0.wireOp",EDGE,"E21.filletArc"),sQuery(id+"F0.wireOp",EDGE,"E22.filletArc"),sQuery(id+"F0.wireOp",EDGE,"E23.filletArc")])]});
            hole(context, id + "F19", {"style" : HoleStyle.SIMPLE, "endStyle" : HoleEndStyle.BLIND, "oppositeDirection" : true, "standardTappedOrClearance" : lookupTablePath({ "standard" : "ANSI", "engagement" : "75%", "pitch" : "20 tpi", "size" : "1/4", "type" : "Tapped" }), "standardBlindInLast" : lookupTablePath({ "standard" : "ANSI", "engagement" : "75%", "pitch" : "20 tpi", "size" : "1/4", "type" : "Tapped" }), "holeDiameter" : 5.1 * mm, "showTappedDepth" : true, "holeDepth" : 15.8 * mm, "tappedDepth" : 12 * mm, "tapClearance" : 3, "locations" : qUnion([Q0]), "scope" : qUnion([Q1]), "majorDiameter" : 6.35 * mm});
        }
    });
